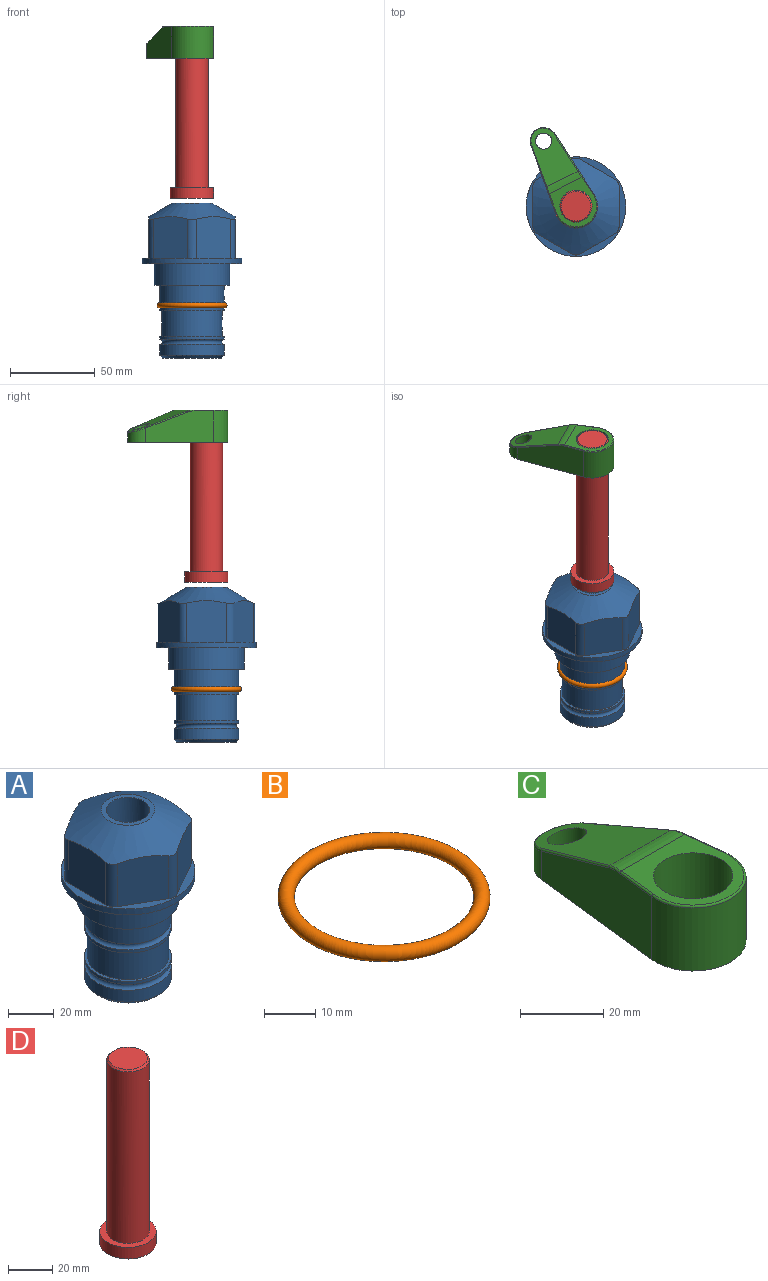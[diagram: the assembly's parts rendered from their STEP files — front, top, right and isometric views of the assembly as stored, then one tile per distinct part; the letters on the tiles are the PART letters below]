
ASSEMBLY  parts=4 mates=2
PART A: 36 faces, bbox 58.7x58.7x91.2 mm
  f0: cylinder r=17.78mm len=35.56mm, axis (0,0,1), area 1670.8mm2, adj f23,f24,f31
  f1: cylinder r=19.05mm len=38.1mm, axis (0,0,1), area 1191.9mm2, adj f26,f27,f30
  f2: plane 58.66x58.66mm, normal (0,0,-1), area 1150.6mm2, adj f3,f28
  f3: cylinder r=29.33mm len=58.66mm, axis (0,0,-1), area 585.1mm2, adj f2,f4
  f4: plane 58.66x58.66mm, normal (0,0,1), area 475.9mm2, adj f3,f5,f6,f7,f8,f9,f10,f11
  f5: plane 24.5x20.32mm, normal (-0.5,0.87,0), area 562.8mm2, adj f4,f15,f16,f17
  f6: plane 24.5x20.32mm, normal (0.5,0.87,0), area 562.8mm2, adj f4,f14,f15,f17
  f7: plane 24.5x23.48mm, normal (1,0,0), area 562.8mm2, adj f4,f13,f14,f17
  f8: plane 24.5x20.32mm, normal (0.5,-0.87,0), area 562.8mm2, adj f4,f12,f13,f17
  f9: plane 24.5x20.32mm, normal (-0.5,-0.87,0), area 562.8mm2, adj f4,f11,f12,f17
  f10: plane 24.5x23.48mm, normal (-1,0,0), area 562.8mm2, adj f4,f11,f16,f17
  f11: cylinder r=5.08mm len=23.01mm, axis (0,0,-1), area 121.2mm2, adj f4,f9,f10,f17
  f12: cylinder r=5.08mm len=23.01mm, axis (0,0,-1), area 121.2mm2, adj f4,f8,f9,f17
  f13: cylinder r=5.08mm len=23.01mm, axis (0,0,-1), area 121.2mm2, adj f4,f7,f8,f17
  f14: cylinder r=5.08mm len=23.01mm, axis (0,0,-1), area 121.2mm2, adj f4,f6,f7,f17
  f15: cylinder r=5.08mm len=23.01mm, axis (0,0,-1), area 121.2mm2, adj f4,f5,f6,f17
  f16: cylinder r=5.08mm len=23.01mm, axis (0,0,-1), area 121.2mm2, adj f4,f5,f10,f17
  f17: cone r=11.73mm half-angle=60deg, axis (0,0,-1), area 2071.8mm2, adj f5,f6,f7,f8,f9,f10,f11,f12
  f18: plane 23.46x23.46mm, normal (0,0,1), area 147.4mm2, adj f17,f35
  f19: plane 34.93x34.93mm, normal (0,0,-1), area 958mm2, adj f29
  f20: cylinder r=19.05mm len=38.1mm, axis (0,0,1), area 760.1mm2, adj f21,f29
  f21: torus R=19.05mm, axis (0,0,1), area 565.3mm2, adj f20,f22
  f22: cylinder r=19.05mm len=38.1mm, axis (0,0,1), area 190mm2, adj f21,f23
  f23: plane 38.1x38.1mm, normal (0,0,1), area 146.9mm2, adj f0,f22
  f24: plane 38.1x38.1mm, normal (0,0,-1), area 146.9mm2, adj f0,f25
  f25: cylinder r=19.05mm len=38.1mm, axis (0,0,1), area 190mm2, adj f24,f26
  f26: torus R=19.05mm, axis (0,0,1), area 565.3mm2, adj f1,f25
  f27: plane 44.45x44.45mm, normal (0,0,-1), area 411.7mm2, adj f1,f28
  f28: cylinder r=22.23mm len=44.45mm, axis (0,0,1), area 1773.5mm2, adj f2,f27
  f29: cone r=19.05mm half-angle=45deg, axis (0,0,1), area 257.5mm2, adj f19,f20
  f30: cylinder r=3.17mm len=6.75mm, axis (-1,0,0), area 128mm2, adj f1,f33
  f31: cylinder r=3.17mm len=6.35mm, axis (-1,0,0), area 102.5mm2, adj f0,f33
  f32: plane 25.4x25.4mm, normal (0,0,1), area 506.7mm2, adj f33
  f33: cylinder r=12.7mm len=66.42mm, axis (0,0,-1), area 5236.2mm2, adj f30,f31,f32,f34
  f34: cone r=9.53mm half-angle=30deg, axis (0,0,-1), area 443.4mm2, adj f33,f35
  f35: cylinder r=9.53mm len=19.05mm, axis (0,0,-1), area 849mm2, adj f18,f34
PART B: 1 faces, bbox 44.7x44.7x3.2 mm
  f0: torus R=19.05mm, axis (0,0,1), area 1193.9mm2
PART C: 44 faces, bbox 27.5x64.5x19.1 mm
  f0: plane 2.3x0.95mm, normal (0,0,-1), area 1mm2, adj f25,f30,f34
  f1: plane 63.5x25.4mm, normal (0,0,-1), area 561.7mm2, adj f2,f3,f4,f5,f6,f7,f19,f20
  f2: cylinder r=12.7mm len=25.4mm, axis (0,0,-1), area 792.2mm2, adj f1,f3,f5,f13
  f3: plane 42.33x18.54mm, normal (0.99,0.11,0), area 647mm2, adj f1,f2,f4,f11,f12,f14
  f4: cylinder r=7.94mm len=15.78mm, axis (0,0,-1), area 158.6mm2, adj f1,f3,f5,f16
  f5: plane 42.33x18.54mm, normal (-0.99,0.11,0), area 647mm2, adj f1,f2,f4,f15,f17,f18
  f6: cylinder r=9.53mm len=19.05mm, axis (0,0,-1), area 1140.1mm2, adj f1,f8
  f7: cylinder r=4.76mm len=10.98mm, axis (0,0,-1), area 276.1mm2, adj f1,f9
  f8: plane 25.83x24.38mm, normal (0,0,1), area 262.2mm2, adj f6,f10,f11,f13,f15
  f9: plane 32.49x20.55mm, normal (0,0.34,0.94), area 489.9mm2, adj f7,f10,f14,f16,f18
  f10: cylinder r=12.7mm len=21.49mm, axis (-1,0,0), area 93.2mm2, adj f8,f9,f12,f17
  f11: cylinder r=0.51mm len=12.34mm, axis (0.11,-0.99,0), area 9.9mm2, adj f3,f8,f12,f13
  f12: bspline ~7.62x1.64mm, area 3.5mm2, adj f3,f10,f11,f14
  f13: torus R=12.19mm, axis (0,0,1), area 33.6mm2, adj f2,f8,f11,f15
  f14: cylinder r=0.51mm len=26.01mm, axis (0.1,-0.93,0.34), area 21.6mm2, adj f3,f9,f12,f16
  f15: cylinder r=0.51mm len=12.34mm, axis (0.11,0.99,0), area 9.9mm2, adj f5,f8,f13,f17
  f16: bspline ~15.78x7.05mm, area 15.7mm2, adj f4,f9,f14,f18
  f17: bspline ~7.62x1.64mm, area 3.5mm2, adj f5,f10,f15,f18
  f18: cylinder r=0.51mm len=26.01mm, axis (0.1,0.93,-0.34), area 21.6mm2, adj f5,f9,f16,f17
  f19: plane 21.6x14.29mm, normal (-0.99,-0.11,0), area 242.6mm2, adj f1,f26,f28,f34,f36,f38
  f20: plane 21.6x14.29mm, normal (0.99,-0.11,0), area 242.6mm2, adj f1,f27,f29,f37,f39,f41
  f21: cylinder r=12.7mm len=14.29mm, axis (0,0,-1), area 173.2mm2, adj f1,f26,f27,f30,f31,f33
  f22: cylinder r=7.94mm len=7.63mm, axis (0,0,-1), area 53.8mm2, adj f1,f28,f29,f42
  f23: plane 2.3x0.95mm, normal (0,0,-1), area 1mm2, adj f25,f33,f37
  f24: plane 17.94x12.32mm, normal (0,-0.34,-0.94), area 191.2mm2, adj f25,f38,f41,f42
  f25: cylinder r=9.53mm len=12.93mm, axis (-1,0,0), area 37.5mm2, adj f0,f23,f24,f31,f36,f39
  f26: cylinder r=1.59mm len=14.29mm, axis (0,0,-1), area 49mm2, adj f1,f19,f21,f32
  f27: cylinder r=1.59mm len=14.29mm, axis (0,0,-1), area 49mm2, adj f1,f20,f21,f35
  f28: cylinder r=1.59mm len=7.28mm, axis (0,0,-1), area 22.1mm2, adj f1,f19,f22,f40
  f29: cylinder r=1.59mm len=7.28mm, axis (0,0,-1), area 22.1mm2, adj f1,f20,f22,f43
  f30: torus R=14.29mm, axis (0,0,1), area 5.8mm2, adj f0,f21,f31,f32
  f31: bspline ~11.06x2.73mm, area 20.8mm2, adj f21,f25,f30,f33
  f32: sphere r=1.59mm, area 5.4mm2, adj f26,f30,f34
  f33: torus R=14.29mm, axis (0,0,1), area 5.8mm2, adj f21,f23,f31,f35
  f34: cylinder r=1.59mm len=1.68mm, axis (-0.11,0.99,0), area 2.4mm2, adj f0,f19,f32,f36
  f35: sphere r=1.59mm, area 5.4mm2, adj f27,f33,f37
  f36: bspline ~5.82x2.33mm, area 7.7mm2, adj f19,f25,f34,f38
  f37: cylinder r=1.59mm len=1.68mm, axis (0.11,0.99,0), area 2.4mm2, adj f20,f23,f35,f39
  f38: cylinder r=1.59mm len=18.33mm, axis (0.1,-0.93,0.34), area 46.7mm2, adj f19,f24,f36,f40
  f39: bspline ~5.82x2.33mm, area 7.7mm2, adj f20,f25,f37,f41
  f40: sphere r=1.59mm, area 3.6mm2, adj f28,f38,f42
  f41: cylinder r=1.59mm len=18.33mm, axis (0.1,0.93,-0.34), area 46.7mm2, adj f20,f24,f39,f43
  f42: bspline ~8.31x1.84mm, area 15.3mm2, adj f22,f24,f40,f43
  f43: sphere r=1.59mm, area 3.6mm2, adj f29,f41,f42
PART D: 6 faces, bbox 25.4x25.4x101.6 mm
  f0: plane 17.46x17.46mm, normal (0,0,1), area 239.5mm2, adj f5
  f1: plane 25.4x25.4mm, normal (0,0,-1), area 506.7mm2, adj f2
  f2: cylinder r=12.7mm len=25.4mm, axis (0,0,1), area 506.7mm2, adj f1,f3
  f3: plane 25.4x25.4mm, normal (0,0,1), area 221.7mm2, adj f2,f4
  f4: cylinder r=9.53mm len=94.46mm, axis (0,0,1), area 5653mm2, adj f3,f5
  f5: cone r=8.73mm half-angle=45deg, axis (0,0,-1), area 64.4mm2, adj f0,f4
PLACE A at identity fixed
PLACE B at identity
PLACE C rot(axis=(0,0,1),26.4deg) t=(0,0,120.98)mm
PLACE D rot(axis=(0,0,1),26.4deg) t=(0,0,66.37)mm
MATE cylindrical D.f2 <-> A.f0  axis (0,0,1) through (0,0,92)mm
MATE fastened C.f2 <-> D.f2  axis (0,0,-1) through (0,0,140.03)mm
